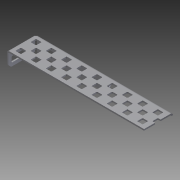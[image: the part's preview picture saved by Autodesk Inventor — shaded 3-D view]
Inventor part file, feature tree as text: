
AUTODESK INVENTOR PART (.ipt)
format: ipt  version: 2012 (Build 160160000, 160)  size: 875,520 bytes
history: native  units: in
note: dims shown in document units (in); Inventor stores cm internally (conversion verified against a paired STEP export)
features: other x1, imported_body x1, plane x1, split x1, extrude x1, fillet x1, sketch x1
ambient origin geometry x8: Origin, YZ Plane, XZ Plane, XY Plane, X Axis, Y Axis, Z Axis, Center Point
feature tree (7):
  parser-record x1  (decoder bookkeeping rows leaked as tree rows — omitted from the tree; the rows remain in map.json)
  imported_body  "Base1"
  plane  "Work Plane1"
  split  "Split1"
  extrude  "Extrusion1"  Depth=1.0in TaperAngle=0.0deg
  fillet  "Fillet1"  Radius=0.375in
  sketch  "Sketch1"  dims[d0=-8.0in d1=1.0in d2=0.0in d3=0.375in]
